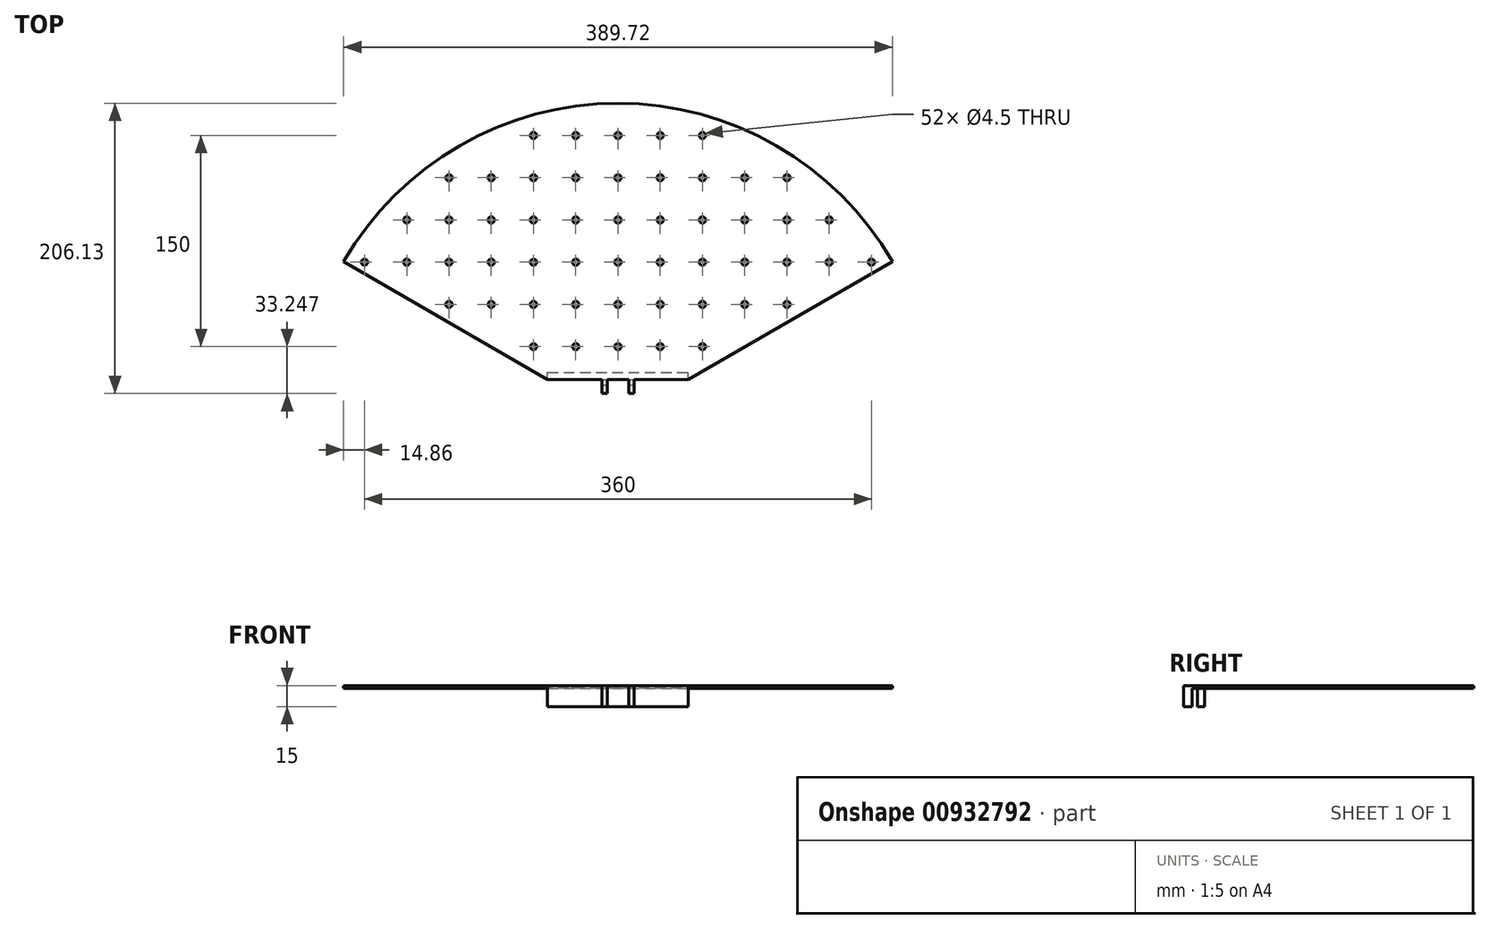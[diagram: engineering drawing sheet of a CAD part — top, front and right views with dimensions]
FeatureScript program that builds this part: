
annotation { "Feature Type Name" : "Feature", "Feature Type Description" : "" }
export const myFeature = defineFeature(function(context is Context, id is Id, definition is map)
    precondition{}
    {
        {
            var Q0;
            Q0=qCreatedBy(makeId("Top.planeOp"),FACE);
            var sketch = newSketch(context, id + "F0", { "sketchPlane" : qUnion([Q0])});
            skArc(sketch, "E0", {"start": v(194.86, 112.5) * mm, "mid": v(0, 225) * mm, "end": v(-194.86, 112.5) * mm});
            skLineSegment(sketch, "E1", {"start": v(-50, 28.87) * mm, "end": v(50, 28.87) * mm});
            skLineSegment(sketch, "E2", {"start": v(-50, 28.87) * mm, "end": v(-194.86, 112.5) * mm});
            skLineSegment(sketch, "E3", {"start": v(50, 28.87) * mm, "end": v(194.86, 112.5) * mm});
            skPoint(sketch, "E4", {"position": v(0, 14.43) * mm});
            skPoint(sketch, "E5.start.orphan", {"position": v(0, -57.74) * mm});
            skSolve(sketch);
        }
        {
            var Q0;
            Q0 = qSketchRegion(id + "F0", true);
            extrude(context, id + "F1", {"entities" : qUnion([Q0]), "depth" : 2 * mm, "offsetDistance" : 25 * mm});
        }
        {
            var Q0;
            Q0=makeQuery(id+"F1.opExtrude","CAP_FACE",FACE,{"disambiguationData":[OSD([sQuery(id+"F0.wireOp",EDGE,"E0"),sQuery(id+"F0.wireOp",EDGE,"E1"),sQuery(id+"F0.wireOp",EDGE,"E2"),sQuery(id+"F0.wireOp",EDGE,"E3")])],"isStart":false});
            var sketch = newSketch(context, id + "F2", { "sketchPlane" : qUnion([Q0])});
            skCircle(sketch, "E6", {"center": v(0, 52.12) * mm, "radius": 2.25 * mm});
            skPoint(sketch, "E6.centerSnap0", {"position": v(0, 28.87) * mm});
            skCircle(sketch, "E7.0.1.0", {"center": v(0, 82.12) * mm, "radius": 2.25 * mm});
            skCircle(sketch, "E7.0.2.0", {"center": v(0, 112.12) * mm, "radius": 2.25 * mm});
            skCircle(sketch, "E7.0.3.0", {"center": v(0, 142.12) * mm, "radius": 2.25 * mm});
            skCircle(sketch, "E7.0.4.0", {"center": v(0, 172.12) * mm, "radius": 2.25 * mm});
            skCircle(sketch, "E7.0.5.0", {"center": v(0, 202.12) * mm, "radius": 2.25 * mm});
            skCircle(sketch, "E7.1.0.0", {"center": v(30, 52.12) * mm, "radius": 2.25 * mm});
            skCircle(sketch, "E7.1.1.0", {"center": v(30, 82.12) * mm, "radius": 2.25 * mm});
            skCircle(sketch, "E7.1.2.0", {"center": v(30, 112.12) * mm, "radius": 2.25 * mm});
            skCircle(sketch, "E7.1.3.0", {"center": v(30, 142.12) * mm, "radius": 2.25 * mm});
            skCircle(sketch, "E7.1.4.0", {"center": v(30, 172.12) * mm, "radius": 2.25 * mm});
            skCircle(sketch, "E7.1.5.0", {"center": v(30, 202.12) * mm, "radius": 2.25 * mm});
            skCircle(sketch, "E7.2.0.0", {"center": v(60, 52.12) * mm, "radius": 2.25 * mm});
            skCircle(sketch, "E7.2.1.0", {"center": v(60, 82.12) * mm, "radius": 2.25 * mm});
            skCircle(sketch, "E7.2.2.0", {"center": v(60, 112.12) * mm, "radius": 2.25 * mm});
            skCircle(sketch, "E7.2.3.0", {"center": v(60, 142.12) * mm, "radius": 2.25 * mm});
            skCircle(sketch, "E7.2.4.0", {"center": v(60, 172.12) * mm, "radius": 2.25 * mm});
            skCircle(sketch, "E7.2.5.0", {"center": v(60, 202.12) * mm, "radius": 2.25 * mm});
            skLineSegment(sketch, "E7.direction1", {"start": v(0, 52.12) * mm, "end": v(30, 52.12) * mm, "construction": true});
            skLineSegment(sketch, "E7.direction2", {"start": v(0, 52.12) * mm, "end": v(0, 82.12) * mm, "construction": true});
            skCircle(sketch, "E8.1.0.0", {"center": v(-30, 202.12) * mm, "radius": 2.25 * mm});
            skCircle(sketch, "E8.1.0.1", {"center": v(-30, 172.12) * mm, "radius": 2.25 * mm});
            skCircle(sketch, "E8.1.0.2", {"center": v(-30, 142.12) * mm, "radius": 2.25 * mm});
            skCircle(sketch, "E8.1.0.3", {"center": v(-30, 112.12) * mm, "radius": 2.25 * mm});
            skCircle(sketch, "E8.1.0.4", {"center": v(-30, 82.12) * mm, "radius": 2.25 * mm});
            skLineSegment(sketch, "E8.1.0.5", {"start": v(-30, 52.12) * mm, "end": v(0, 52.12) * mm, "construction": true});
            skCircle(sketch, "E8.1.0.6", {"center": v(-30, 52.12) * mm, "radius": 2.25 * mm});
            skCircle(sketch, "E8.2.0.0", {"center": v(-60, 202.12) * mm, "radius": 2.25 * mm});
            skCircle(sketch, "E8.2.0.1", {"center": v(-60, 172.12) * mm, "radius": 2.25 * mm});
            skCircle(sketch, "E8.2.0.2", {"center": v(-60, 142.12) * mm, "radius": 2.25 * mm});
            skCircle(sketch, "E8.2.0.3", {"center": v(-60, 112.12) * mm, "radius": 2.25 * mm});
            skCircle(sketch, "E8.2.0.4", {"center": v(-60, 82.12) * mm, "radius": 2.25 * mm});
            skLineSegment(sketch, "E8.2.0.5", {"start": v(-60, 52.12) * mm, "end": v(-30, 52.12) * mm, "construction": true});
            skCircle(sketch, "E8.2.0.6", {"center": v(-60, 52.12) * mm, "radius": 2.25 * mm});
            skLineSegment(sketch, "E8.direction1", {"start": v(0, 202.12) * mm, "end": v(-30, 202.12) * mm, "construction": true});
            skCircle(sketch, "E9.1.0.0", {"center": v(-90, 112.12) * mm, "radius": 2.25 * mm});
            skCircle(sketch, "E9.1.0.1", {"center": v(-90, 82.12) * mm, "radius": 2.25 * mm});
            skCircle(sketch, "E9.1.0.2", {"center": v(-90, 142.12) * mm, "radius": 2.25 * mm});
            skCircle(sketch, "E9.1.0.3", {"center": v(-90, 172.12) * mm, "radius": 2.25 * mm});
            skCircle(sketch, "E9.2.0.0", {"center": v(-120, 112.12) * mm, "radius": 2.25 * mm});
            skCircle(sketch, "E9.2.0.1", {"center": v(-120, 82.12) * mm, "radius": 2.25 * mm});
            skCircle(sketch, "E9.2.0.2", {"center": v(-120, 142.12) * mm, "radius": 2.25 * mm});
            skCircle(sketch, "E9.2.0.3", {"center": v(-120, 172.12) * mm, "radius": 2.25 * mm});
            skLineSegment(sketch, "E9.direction1", {"start": v(-60, 112.12) * mm, "end": v(-90, 112.12) * mm, "construction": true});
            skCircle(sketch, "E10.1.0.0", {"center": v(90, 112.12) * mm, "radius": 2.25 * mm});
            skCircle(sketch, "E10.1.0.1", {"center": v(90, 82.12) * mm, "radius": 2.25 * mm});
            skCircle(sketch, "E10.1.0.2", {"center": v(90, 142.12) * mm, "radius": 2.25 * mm});
            skCircle(sketch, "E10.1.0.3", {"center": v(90, 172.12) * mm, "radius": 2.25 * mm});
            skCircle(sketch, "E10.2.0.0", {"center": v(120, 112.12) * mm, "radius": 2.25 * mm});
            skCircle(sketch, "E10.2.0.1", {"center": v(120, 82.12) * mm, "radius": 2.25 * mm});
            skCircle(sketch, "E10.2.0.2", {"center": v(120, 142.12) * mm, "radius": 2.25 * mm});
            skCircle(sketch, "E10.2.0.3", {"center": v(120, 172.12) * mm, "radius": 2.25 * mm});
            skLineSegment(sketch, "E10.direction1", {"start": v(60, 112.12) * mm, "end": v(90, 112.12) * mm, "construction": true});
            skCircle(sketch, "E11.1.0.0", {"center": v(-150, 142.12) * mm, "radius": 2.25 * mm});
            skCircle(sketch, "E11.1.0.1", {"center": v(-150, 112.12) * mm, "radius": 2.25 * mm});
            skLineSegment(sketch, "E11.direction1", {"start": v(-120, 142.12) * mm, "end": v(-150, 142.12) * mm, "construction": true});
            skCircle(sketch, "E12.1.0.0", {"center": v(150, 142.12) * mm, "radius": 2.25 * mm});
            skCircle(sketch, "E12.1.0.1", {"center": v(150, 112.12) * mm, "radius": 2.25 * mm});
            skLineSegment(sketch, "E12.direction1", {"start": v(120, 142.12) * mm, "end": v(150, 142.12) * mm, "construction": true});
            skCircle(sketch, "E13.1.0.0", {"center": v(180, 112.12) * mm, "radius": 2.25 * mm});
            skLineSegment(sketch, "E13.direction1", {"start": v(150, 112.12) * mm, "end": v(180, 112.12) * mm, "construction": true});
            skCircle(sketch, "E14.1.0.0", {"center": v(-180, 112.12) * mm, "radius": 2.25 * mm});
            skLineSegment(sketch, "E14.direction1", {"start": v(-150, 112.12) * mm, "end": v(-180, 112.12) * mm, "construction": true});
            skSolve(sketch);
        }
        {
            var Q0;
            Q0 = qSketchRegion(id + "F2", true);
            extrude(context, id + "F3", {"entities" : qUnion([Q0]), "operationType" : NewBodyOperationType.REMOVE, "oppositeDirection" : true, "depth" : 25 * mm, "offsetDistance" : 25 * mm});
        }
        {
            var Q0;
            Q0=makeQuery(id+"F1.opExtrude","SWEPT_FACE",FACE,{"disambiguationData":[OSD([sQuery(id+"F0.wireOp",EDGE,"E1")])]});
            var sketch = newSketch(context, id + "F4", { "sketchPlane" : qUnion([Q0])});
            skLineSegment(sketch, "E15.bottom", {"start": v(-11.5, 2) * mm, "end": v(-7.5, 2) * mm});
            skLineSegment(sketch, "E15.top", {"start": v(-11.5, 0) * mm, "end": v(-7.5, 0) * mm});
            skLineSegment(sketch, "E15.left", {"start": v(-11.5, 2) * mm, "end": v(-11.5, 0) * mm});
            skLineSegment(sketch, "E15.right", {"start": v(-7.5, 2) * mm, "end": v(-7.5, 0) * mm});
            skLineSegment(sketch, "E16.bottom", {"start": v(7.5, 2) * mm, "end": v(11.5, 2) * mm});
            skLineSegment(sketch, "E16.top", {"start": v(7.5, 0) * mm, "end": v(11.5, 0) * mm});
            skLineSegment(sketch, "E16.left", {"start": v(7.5, 2) * mm, "end": v(7.5, 0) * mm});
            skLineSegment(sketch, "E16.right", {"start": v(11.5, 2) * mm, "end": v(11.5, 0) * mm});
            skSolve(sketch);
        }
        {
            var Q0;
            Q0 = qSketchRegion(id + "F4", true);
            extrude(context, id + "F5", {"entities" : qUnion([Q0]), "operationType" : NewBodyOperationType.ADD, "depth" : 10 * mm, "offsetDistance" : 25 * mm});
        }
        {
            var Q0;
            Q0=makeQuery(id+"F5.boolean.opBoolean","MERGE",FACE,{"derivedFrom":[makeQuery(id+"F1.opExtrude","CAP_FACE",FACE,{"disambiguationData":[OSD([sQuery(id+"F0.wireOp",EDGE,"E0"),sQuery(id+"F0.wireOp",EDGE,"E1"),sQuery(id+"F0.wireOp",EDGE,"E2"),sQuery(id+"F0.wireOp",EDGE,"E3")])],"isStart":true}),makeQuery(id+"F5.opExtrude","SWEPT_FACE",FACE,{"disambiguationData":[OSD([sQuery(id+"F4.wireOp",EDGE,"E15.top")])]}),makeQuery(id+"F5.opExtrude","SWEPT_FACE",FACE,{"disambiguationData":[OSD([sQuery(id+"F4.wireOp",EDGE,"E16.top")])]})]});
            var sketch = newSketch(context, id + "F6", { "sketchPlane" : qUnion([Q0])});
            skLineSegment(sketch, "E17.bottom", {"start": v(-50, -28.87) * mm, "end": v(50, -28.87) * mm});
            skLineSegment(sketch, "E17.top", {"start": v(-50, -33.87) * mm, "end": v(50, -33.87) * mm});
            skLineSegment(sketch, "E17.left", {"start": v(-50, -28.87) * mm, "end": v(-50, -33.87) * mm});
            skLineSegment(sketch, "E17.right", {"start": v(50, -28.87) * mm, "end": v(50, -33.87) * mm});
            skLineSegment(sketch, "E18.bottom", {"start": v(-11.5, -18.87) * mm, "end": v(-7.5, -18.87) * mm});
            skLineSegment(sketch, "E18.top", {"start": v(-11.5, -24.87) * mm, "end": v(-7.5, -24.87) * mm});
            skLineSegment(sketch, "E18.left", {"start": v(-11.5, -18.87) * mm, "end": v(-11.5, -24.87) * mm});
            skLineSegment(sketch, "E18.right", {"start": v(-7.5, -18.87) * mm, "end": v(-7.5, -24.87) * mm});
            skLineSegment(sketch, "E19.bottom", {"start": v(7.5, -18.87) * mm, "end": v(11.5, -18.87) * mm});
            skLineSegment(sketch, "E19.top", {"start": v(7.5, -24.87) * mm, "end": v(11.5, -24.87) * mm});
            skLineSegment(sketch, "E19.left", {"start": v(7.5, -18.87) * mm, "end": v(7.5, -24.87) * mm});
            skLineSegment(sketch, "E19.right", {"start": v(11.5, -18.87) * mm, "end": v(11.5, -24.87) * mm});
            skSolve(sketch);
        }
        {
            var Q0;
            Q0 = qSketchRegion(id + "F6", true);
            extrude(context, id + "F7", {"entities" : qUnion([Q0]), "operationType" : NewBodyOperationType.ADD, "depth" : 13 * mm, "offsetDistance" : 25 * mm});
        }
    });
